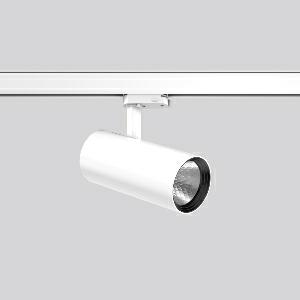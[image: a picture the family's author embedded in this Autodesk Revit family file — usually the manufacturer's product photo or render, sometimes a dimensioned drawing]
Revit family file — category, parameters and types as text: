
# Revit family: deecos_s_mini_742205_002_b969
name_source: partatom
category: Lighting Fixtures
units: mm (PartAtom-declared; Revit-internal decimal feet)

## family parameters
Cut with Voids When Loaded = No
Host = Face
Light Source = No
Part Type = Normal
Room Calculation Point = No
Round Connector Dimension = Use Diameter
Shared = No

## types (1)
- DEECOS S mini (1 x LED Modul 930, 3650 lm, 3000)
    Apparent Load = 29 VA
    Approval mark = CE
    CIE Flux Codes = 95 99 100 100 100
    Color Rendering = 90
    Color Temperature = 3000
    Default Elevation = 1800 mm
    Description = Series: DEECOS S mini
LED surface-mounted projector in modern design with no visible cooling ribs. Housing: die-cast aluminium, powder-coated. Rotation range: 356°. Swivel range: 90°. Black plastic ring and recessed LED to prevent glare from the side. Optical assembly with reflector made of MIRO-Silver with 98% total light reflection for outstanding efficiency - can be changed without tools. Best colour rendering index Ra>90. With multi adaptor for 3-circuit tracks 230 V. Suitable for Track on ceiling, Wall track. High quality converter without flickering and stroboscopic effect. The following accessories can be mounted without use of tools: interchangeable lenses, decorative glasses, honeycomb louvre, clear and frosted diffusers, white interchangeable plastic ring. 
Colour: traffic white, matt (RAL 9016)
Diameter: 87 mm
Height: 214 mm
Lamp: LED
Socket: without socket
Colour temperature: 3000K
Colour rendering index (CRI): 92
System power: 29 W
Rated luminous flux: 3650 lm
Luminous efficiency: 126 lm/W
Control gear: Regulated power supply
Protection class: I
Type of protection: IP 20
    Height = 214 mm
    Lamp = 1 x LED Modul 930
    Lamp Light Flux = 3650 lm
    Lamp count = 1
    Length = 87 mm
    Lifetime = 50000 h
    Luminous efficacy = 126 lm/W
    Manufacturer = RZB
    ModVariant = No
    Model = 742205.002
    Mounting Place = Ceiling
    Mounting Type = Rail mounted
    Number of Poles = 1
    OnlyDefault = Yes
    Power Factor = 1
    Product Name = DEECOS S mini
    Product group = Track mounted projectors
    ProductGroupID = 301
    Protection Class = Protection class I
    Protection Degree = IP 20
    RLX_Detail_Level = 1
    RLX_Emergency_Light_Flux = 0 lm
    RLX_Emergency_Type = 0
    RLX_Emergency_Type_DB = No
    RlxData = <blob elided: 35313 chars, md5=cfa028fd>
    Socket = socket
    Standby Power = 0 W
    System Light Flux = 3650 lm
    System Power = 29 W
    Type Comments = Product without accessories
    Type Image = 741926.002.jpg
    URL = http://relux.com
    VarID = ---
    Voltage = 230 V
    Voltage Range = 220-240 V
    Weight = 0.00 kg
    Width = 0 mm  [stored 0 ft]

note: [stored X ft] marks values corroborated as IEEE doubles in the binary element streams (Revit-internal decimal feet)

## geometry (parser evidence)
native form markers: Blend x4, Sweep x13
no freeform markers — native parametric forms only
